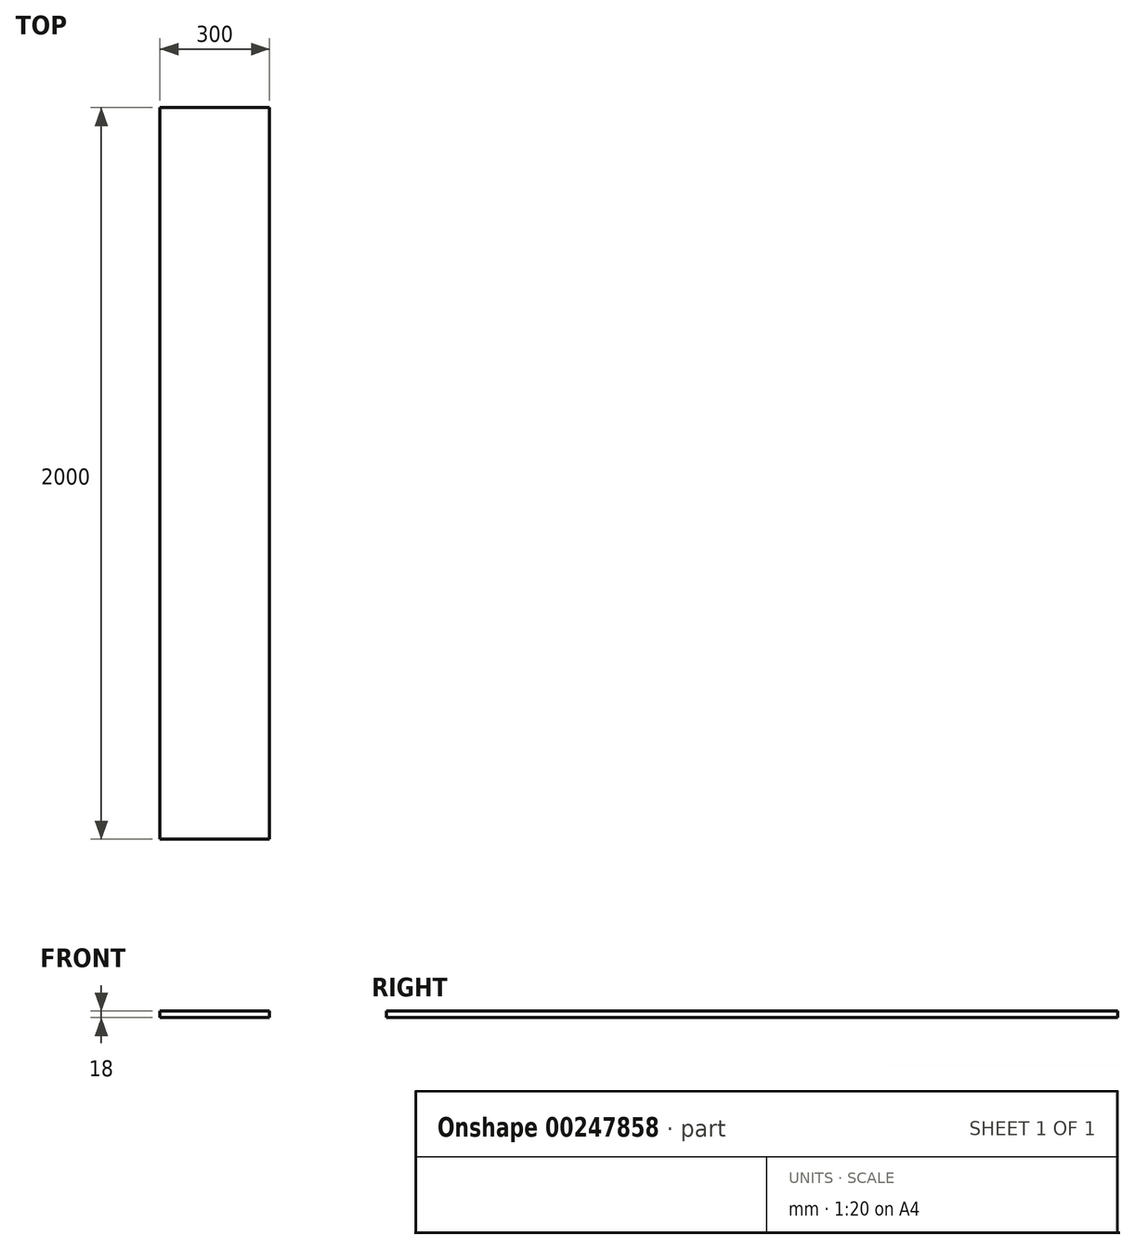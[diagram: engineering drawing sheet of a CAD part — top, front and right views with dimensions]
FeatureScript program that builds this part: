
annotation { "Feature Type Name" : "Feature", "Feature Type Description" : "" }
export const myFeature = defineFeature(function(context is Context, id is Id, definition is map)
    precondition{}
    {
        {
            var Q0;
            Q0=qCreatedBy(makeId("Top.planeOp"),FACE);
            var sketch = newSketch(context, id + "F1", { "sketchPlane" : qUnion([Q0])});
            skLineSegment(sketch, "E0.bottom", {"start": v(0, 0) * mm, "end": v(300, 0) * mm});
            skLineSegment(sketch, "E0.top", {"start": v(0, 2000) * mm, "end": v(300, 2000) * mm});
            skLineSegment(sketch, "E0.left", {"start": v(0, 0) * mm, "end": v(0, 2000) * mm});
            skLineSegment(sketch, "E0.right", {"start": v(300, 0) * mm, "end": v(300, 2000) * mm});
            skSolve(sketch);
        }
        {
            var Q0;
            Q0=makeQuery(id+"F1.imprint","IMPRINT",FACE,{"disambiguationData":[TD([[makeQuery(id+"F1.imprint","IMPRINT",EDGE,{"derivedFrom":sQuery(id+"F1.wireOp",EDGE,"E0.bottom")}),1.0]])]});
            extrude(context, id + "F0", {"entities" : qUnion([Q0]), "depth" : 18 * mm});
        }
    });
